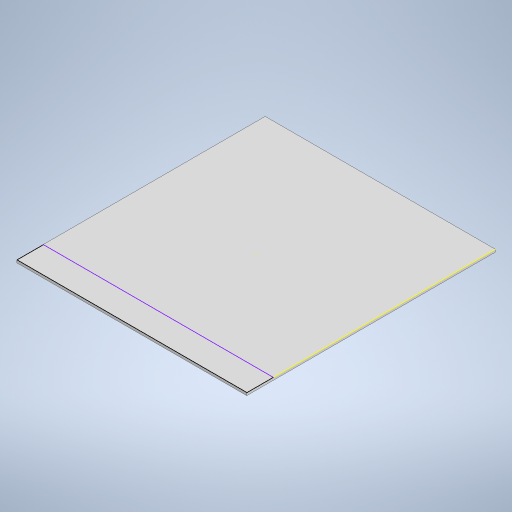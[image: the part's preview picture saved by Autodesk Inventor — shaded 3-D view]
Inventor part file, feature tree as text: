
AUTODESK INVENTOR PART (.ipt)
format: ipt  version: 2023 (Build 270158000, 158)  size: 205,824 bytes
history: native  units: mm
features: sketch x2, extrude x1
ambient origin geometry x8: Origin, YZ Plane, XZ Plane, XY Plane, X Axis, Y Axis, Z Axis, Center Point
bodies: Solid1 (feature_tree)
feature tree (3):
  extrude  "Extrusion1"  Depth=100.0mm
  sketch  "Sketch2"  dims[d2=1.2mm d3=0.0mm]
  sketch  "Sketch1"  dims[d0=108.0mm d1=100.0mm]
